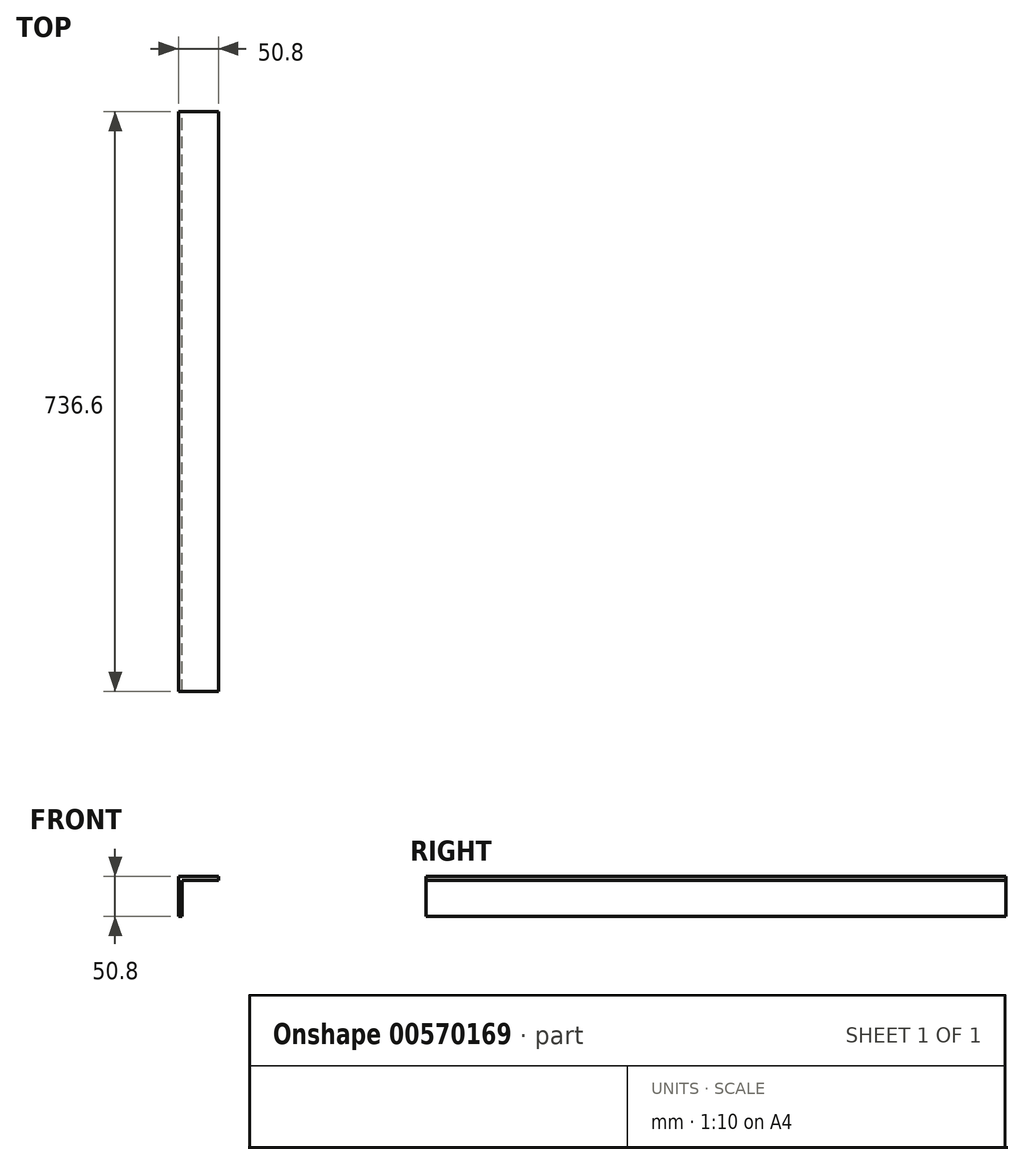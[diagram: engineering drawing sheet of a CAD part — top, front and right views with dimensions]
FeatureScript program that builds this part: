
annotation { "Feature Type Name" : "Feature", "Feature Type Description" : "" }
export const myFeature = defineFeature(function(context is Context, id is Id, definition is map)
    precondition{}
    {
        {
            var Q0;
            Q0=qCreatedBy(makeId("Front.planeOp"),FACE);
            var sketch = newSketch(context, id + "F0", { "sketchPlane" : qUnion([Q0])});
            skLineSegment(sketch, "E0", {"start": v(0, 0) * mm, "end": v(0, 50.8) * mm});
            skLineSegment(sketch, "E1", {"start": v(0, 50.8) * mm, "end": v(50.8, 50.8) * mm});
            skLineSegment(sketch, "E2", {"start": v(50.8, 50.8) * mm, "end": v(50.8, 46.04) * mm});
            skLineSegment(sketch, "E3", {"start": v(50.8, 46.04) * mm, "end": v(4.76, 46.04) * mm});
            skLineSegment(sketch, "E4", {"start": v(4.76, 46.04) * mm, "end": v(4.76, 0) * mm});
            skLineSegment(sketch, "E5", {"start": v(4.76, 0) * mm, "end": v(0, 0) * mm});
            skSolve(sketch);
        }
        {
            var Q0;
            Q0 = qSketchRegion(id + "F0", true);
            extrude(context, id + "F1", {"entities" : qUnion([Q0]), "depth" : 736.6 * mm, "offsetDistance" : 25.4 * mm});
        }
    });
